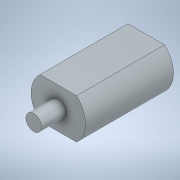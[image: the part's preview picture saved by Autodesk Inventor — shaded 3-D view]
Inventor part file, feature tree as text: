
AUTODESK INVENTOR PART (.ipt)
format: ipt  version: 2020 (Build 240168000, 168)  size: 106,496 bytes
history: native  units: mm
features: extrude x2, sketch x2
ambient origin geometry x8: Origin, YZ Plane, XZ Plane, XY Plane, X Axis, Y Axis, Z Axis, Center Point
bodies: Solid1 (feature_tree)
feature tree (4):
  extrude  "Extrusion1"  Depth=12.8mm
  extrude  "Extrusion2"  Depth=7.8mm
  sketch  "Sketch1"  dims[d0=17.3mm d1=12.8mm]
  sketch  "Sketch2"  dims[d2=28.0mm d3=0.0mm d4=5.0mm d5=7.8mm d6=0.0mm]
